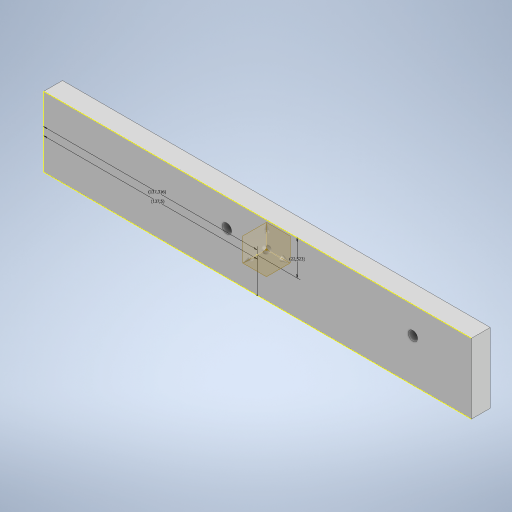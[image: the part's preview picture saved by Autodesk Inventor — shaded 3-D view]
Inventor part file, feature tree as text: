
AUTODESK INVENTOR PART (.ipt)
format: ipt  version: 2024 (Build 280153000, 153)  size: 237,056 bytes
history: native  units: mm
features: other x6, sketch x1
ambient origin geometry x8: Origin, YZ Plane, XZ Plane, XY Plane, X Axis, Y Axis, Z Axis, Center Point
bodies: Body1 (feature_tree)
feature tree (7):
  other  "BORDE_2"
  other  "Generador_de_Piezas.ipt"
  other  "Desplazar cuerpo1"
  sketch  "Boceto1"  dims[d0=10.0mm d1=-462.745mm d2=-2387.573mm d3=0.0mm d4=22.523445mm d5=137.316126mm d6=137.5mm d7=0.184mm d8=0.023mm d9=0.0mm]
  other  "Desplazar cuerpo2"
  other  "BORDE_2::Generador_de_Piezas.ipt"
  other  "OperaciónIdentificador1"
